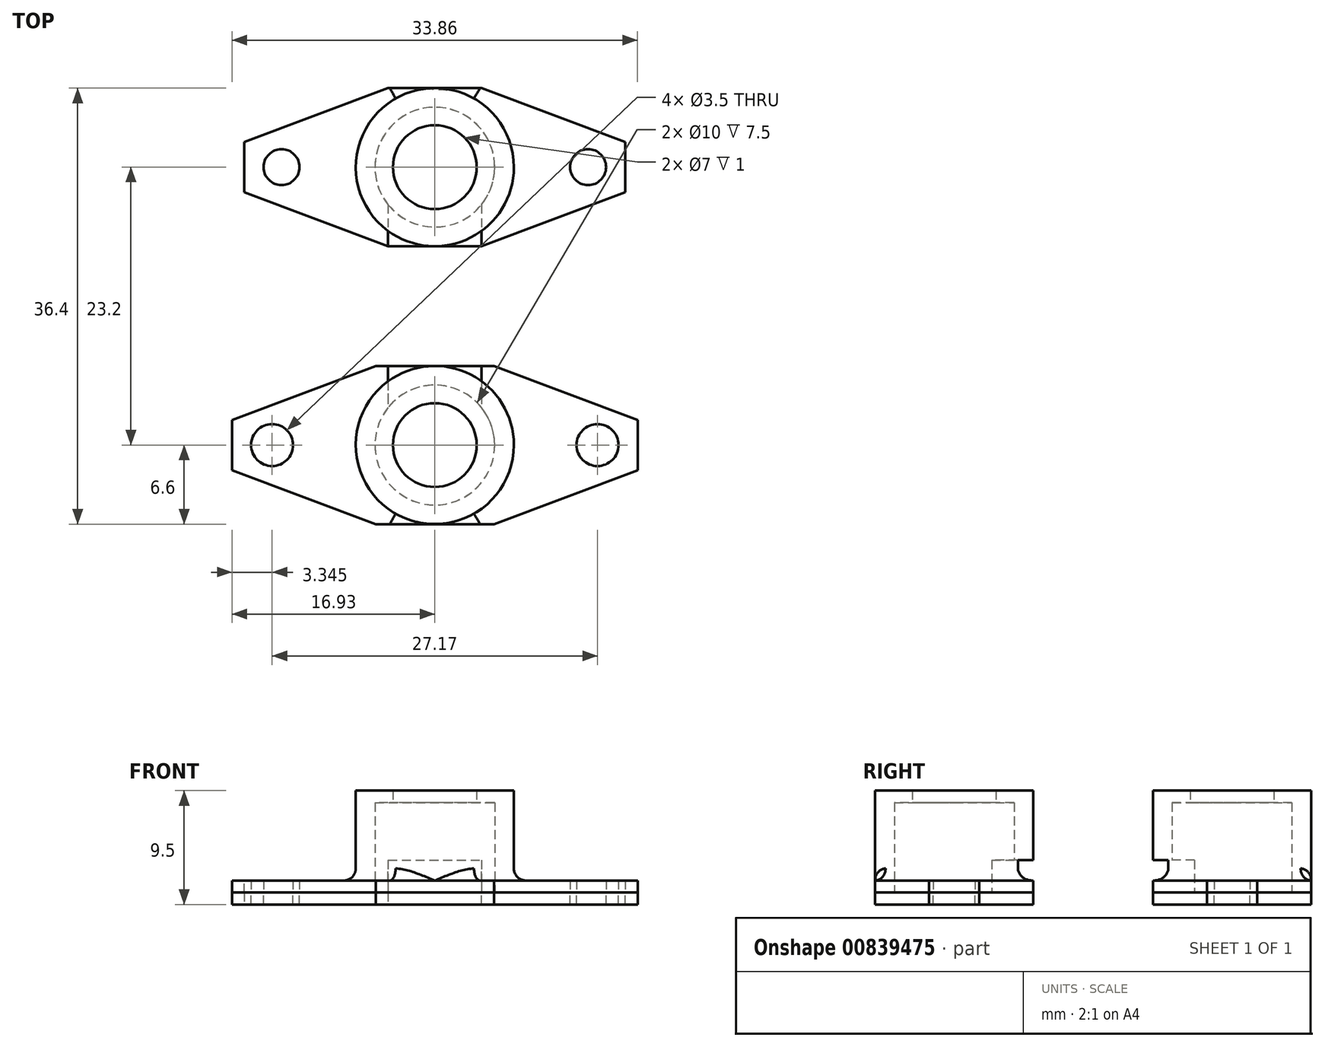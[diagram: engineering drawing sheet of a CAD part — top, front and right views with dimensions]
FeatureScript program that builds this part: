
annotation { "Feature Type Name" : "Feature", "Feature Type Description" : "" }
export const myFeature = defineFeature(function(context is Context, id is Id, definition is map)
    precondition{}
    {
        {
            var Q0;
            Q0=qCreatedBy(makeId("Top.planeOp"),FACE);
            var sketch = newSketch(context, id + "F0", { "sketchPlane" : qUnion([Q0])});
            skLineSegment(sketch, "E0.bottom", {"start": v(-15.9, 5) * mm, "end": v(15.9, 5) * mm});
            skLineSegment(sketch, "E0.top", {"start": v(-15.9, 18.2) * mm, "end": v(15.9, 18.2) * mm});
            skLineSegment(sketch, "E0.left", {"start": v(-15.9, 5) * mm, "end": v(-15.9, 18.2) * mm});
            skLineSegment(sketch, "E0.right", {"start": v(15.9, 5) * mm, "end": v(15.9, 18.2) * mm});
            skCircle(sketch, "E1", {"center": v(-12.8, 11.6) * mm, "radius": 1.5 * mm});
            skCircle(sketch, "E2", {"center": v(12.8, 11.6) * mm, "radius": 1.5 * mm});
            skCircle(sketch, "E3", {"center": v(-13.59, -11.6) * mm, "radius": 1.75 * mm});
            skCircle(sketch, "E4", {"center": v(13.59, -11.6) * mm, "radius": 1.75 * mm});
            skCircle(sketch, "E5", {"center": v(0, -11.6) * mm, "radius": 5 * mm});
            skCircle(sketch, "E6", {"center": v(0, 11.6) * mm, "radius": 5 * mm});
            skPoint(sketch, "E7", {"position": v(-15.9, 11.6) * mm});
            skLineSegment(sketch, "E8.bottom", {"start": v(-16.94, -18.2) * mm, "end": v(16.94, -18.2) * mm});
            skLineSegment(sketch, "E8.top", {"start": v(-16.94, -5) * mm, "end": v(16.94, -5) * mm});
            skLineSegment(sketch, "E8.left", {"start": v(-16.94, -18.2) * mm, "end": v(-16.94, -5) * mm});
            skLineSegment(sketch, "E8.right", {"start": v(16.94, -18.2) * mm, "end": v(16.94, -5) * mm});
            skCircle(sketch, "E9", {"center": v(0, 11.6) * mm, "radius": 6.6 * mm});
            skCircle(sketch, "E10", {"center": v(0, -11.6) * mm, "radius": 6.6 * mm});
            skSolve(sketch);
        }
        {
            var Q0;
            Q0=makeQuery(id+"F0.imprint","IMPRINT",FACE,{"disambiguationData":[TD([[makeQuery(id+"F0.imprint","IMPRINT",EDGE,{"derivedFrom":sQuery(id+"F0.wireOp",EDGE,"E0.bottom")}),1.0]])]});
            var Q1;
            Q1=makeQuery(id+"F0.imprint","IMPRINT",FACE,{"disambiguationData":[TD([[makeQuery(id+"F0.imprint","IMPRINT",EDGE,{"derivedFrom":sQuery(id+"F0.wireOp",EDGE,"E3")}),-1.0]])]});
            var Q2;
            Q2=makeQuery(id+"F0.imprint","IMPRINT",FACE,{"disambiguationData":[TD([[makeQuery(id+"F0.imprint","IMPRINT",EDGE,{"derivedFrom":sQuery(id+"F0.wireOp",EDGE,"E6")}),-1.0]])]});
            var Q3;
            Q3=makeQuery(id+"F0.imprint","IMPRINT",FACE,{"disambiguationData":[TD([[makeQuery(id+"F0.imprint","IMPRINT",EDGE,{"derivedFrom":sQuery(id+"F0.wireOp",EDGE,"E5")}),-1.0]])]});
            var Q4;
            Q4=makeQuery(id+"F0.imprint","IMPRINT",FACE,{"disambiguationData":[TD([[makeQuery(id+"F0.imprint","IMPRINT",EDGE,{"derivedFrom":sQuery(id+"F0.wireOp",EDGE,"E4")}),-1.0]])]});
            extrude(context, id + "F1", {"entities" : qUnion([Q0, Q1, Q2, Q3, Q4]), "depth" : 1 * mm, "offsetDistance" : 25 * mm});
        }
        {
            var Q0;
            Q0=makeQuery(id+"F1.opExtrude","SWEPT_EDGE",EDGE,{"disambiguationData":[OSD([sQuery(id+"F0.wireOp",EDGE,"E0.top"),sQuery(id+"F0.wireOp",EDGE,"E0.left")])]});
            var Q1;
            Q1=makeQuery(id+"F1.opExtrude","SWEPT_EDGE",EDGE,{"disambiguationData":[OSD([sQuery(id+"F0.wireOp",EDGE,"E0.bottom"),sQuery(id+"F0.wireOp",EDGE,"E0.left")])]});
            var Q2;
            Q2=makeQuery(id+"F1.opExtrude","SWEPT_EDGE",EDGE,{"disambiguationData":[OSD([sQuery(id+"F0.wireOp",EDGE,"E8.top"),sQuery(id+"F0.wireOp",EDGE,"E8.left")])]});
            var Q3;
            Q3=makeQuery(id+"F1.opExtrude","SWEPT_EDGE",EDGE,{"disambiguationData":[OSD([sQuery(id+"F0.wireOp",EDGE,"E8.bottom"),sQuery(id+"F0.wireOp",EDGE,"E8.left")])]});
            var Q4;
            Q4=makeQuery(id+"F1.opExtrude","SWEPT_EDGE",EDGE,{"disambiguationData":[OSD([sQuery(id+"F0.wireOp",EDGE,"E0.top"),sQuery(id+"F0.wireOp",EDGE,"E0.right")])]});
            var Q5;
            Q5=makeQuery(id+"F1.opExtrude","SWEPT_EDGE",EDGE,{"disambiguationData":[OSD([sQuery(id+"F0.wireOp",EDGE,"E0.bottom"),sQuery(id+"F0.wireOp",EDGE,"E0.right")])]});
            var Q6;
            Q6=makeQuery(id+"F1.opExtrude","SWEPT_EDGE",EDGE,{"disambiguationData":[OSD([sQuery(id+"F0.wireOp",EDGE,"E8.top"),sQuery(id+"F0.wireOp",EDGE,"E8.right")])]});
            var Q7;
            Q7=makeQuery(id+"F1.opExtrude","SWEPT_EDGE",EDGE,{"disambiguationData":[OSD([sQuery(id+"F0.wireOp",EDGE,"E8.bottom"),sQuery(id+"F0.wireOp",EDGE,"E8.right")])]});
            chamfer(context, id + "F2", {"entities" : qUnion([Q0, Q1, Q2, Q3, Q4, Q5, Q6, Q7]), "chamferType" : ChamferType.TWO_OFFSETS, "width1" : 4.5 * mm, "oppositeDirection" : false, "width2" : 12 * mm, "tangentPropagation" : true});
        }
        {
            var Q0;
            Q0=makeQuery(id+"F0.imprint","IMPRINT",FACE,{"disambiguationData":[TD([[makeQuery(id+"F0.imprint","IMPRINT",EDGE,{"derivedFrom":sQuery(id+"F0.wireOp",EDGE,"E5")}),-1.0]])]});
            var Q1;
            Q1=makeQuery(id+"F0.imprint","IMPRINT",FACE,{"disambiguationData":[TD([[makeQuery(id+"F0.imprint","IMPRINT",EDGE,{"derivedFrom":sQuery(id+"F0.wireOp",EDGE,"E6")}),-1.0]])]});
            extrude(context, id + "F3", {"entities" : qUnion([Q0, Q1]), "operationType" : NewBodyOperationType.ADD, "depth" : 7.5 * mm, "offsetDistance" : 25 * mm});
        }
        {
            var Q0;
            Q0=makeQuery(id+"F3.boolean.opBoolean","INTERSECT",EDGE,{"disambiguationData":[OD(1.0)],"derivedFrom":[makeQuery(id+"F1.opExtrude","CAP_FACE",FACE,{"disambiguationData":[OSD([sQuery(id+"F0.wireOp",EDGE,"E3"),sQuery(id+"F0.wireOp",EDGE,"E4"),sQuery(id+"F0.wireOp",EDGE,"E5"),sQuery(id+"F0.wireOp",EDGE,"E8.bottom"),sQuery(id+"F0.wireOp",EDGE,"E8.top"),sQuery(id+"F0.wireOp",EDGE,"E8.left"),sQuery(id+"F0.wireOp",EDGE,"E8.right")])],"isStart":false}),makeQuery(id+"F3.opExtrude","SWEPT_FACE",FACE,{"disambiguationData":[OSD([sQuery(id+"F0.wireOp",EDGE,"E10")])]})]});
            var Q1;
            Q1=makeQuery(id+"F3.boolean.opBoolean","INTERSECT",EDGE,{"disambiguationData":[OD(0.0)],"derivedFrom":[makeQuery(id+"F1.opExtrude","CAP_FACE",FACE,{"disambiguationData":[OSD([sQuery(id+"F0.wireOp",EDGE,"E3"),sQuery(id+"F0.wireOp",EDGE,"E4"),sQuery(id+"F0.wireOp",EDGE,"E5"),sQuery(id+"F0.wireOp",EDGE,"E8.bottom"),sQuery(id+"F0.wireOp",EDGE,"E8.top"),sQuery(id+"F0.wireOp",EDGE,"E8.left"),sQuery(id+"F0.wireOp",EDGE,"E8.right")])],"isStart":false}),makeQuery(id+"F3.opExtrude","SWEPT_FACE",FACE,{"disambiguationData":[OSD([sQuery(id+"F0.wireOp",EDGE,"E10")])]})]});
            var Q2;
            Q2=makeQuery(id+"F3.boolean.opBoolean","INTERSECT",EDGE,{"disambiguationData":[OD(0.0)],"derivedFrom":[makeQuery(id+"F1.opExtrude","CAP_FACE",FACE,{"disambiguationData":[OSD([sQuery(id+"F0.wireOp",EDGE,"E0.bottom"),sQuery(id+"F0.wireOp",EDGE,"E0.top"),sQuery(id+"F0.wireOp",EDGE,"E0.left"),sQuery(id+"F0.wireOp",EDGE,"E0.right"),sQuery(id+"F0.wireOp",EDGE,"E1"),sQuery(id+"F0.wireOp",EDGE,"E2"),sQuery(id+"F0.wireOp",EDGE,"E6")])],"isStart":false}),makeQuery(id+"F3.opExtrude","SWEPT_FACE",FACE,{"disambiguationData":[OSD([sQuery(id+"F0.wireOp",EDGE,"E9")])]})]});
            var Q3;
            Q3=makeQuery(id+"F3.boolean.opBoolean","INTERSECT",EDGE,{"disambiguationData":[OD(1.0)],"derivedFrom":[makeQuery(id+"F1.opExtrude","CAP_FACE",FACE,{"disambiguationData":[OSD([sQuery(id+"F0.wireOp",EDGE,"E0.bottom"),sQuery(id+"F0.wireOp",EDGE,"E0.top"),sQuery(id+"F0.wireOp",EDGE,"E0.left"),sQuery(id+"F0.wireOp",EDGE,"E0.right"),sQuery(id+"F0.wireOp",EDGE,"E1"),sQuery(id+"F0.wireOp",EDGE,"E2"),sQuery(id+"F0.wireOp",EDGE,"E6")])],"isStart":false}),makeQuery(id+"F3.opExtrude","SWEPT_FACE",FACE,{"disambiguationData":[OSD([sQuery(id+"F0.wireOp",EDGE,"E9")])]})]});
            fillet(context, id + "F4", {"entities" : qUnion([Q0, Q1, Q2, Q3]), "radius" : 1 * mm, "tangentPropagation" : true, "allowEdgeOverflow" : false});
        }
        {
            var Q0;
            Q0=makeQuery(id+"F3.opExtrude","CAP_FACE",FACE,{"disambiguationData":[OSD([sQuery(id+"F0.wireOp",EDGE,"E6"),sQuery(id+"F0.wireOp",EDGE,"E9")])],"isStart":false});
            var sketch = newSketch(context, id + "F5", { "sketchPlane" : qUnion([Q0])});
            skCircle(sketch, "E11.0", {"center": v(0, 11.6) * mm, "radius": 6.6 * mm});
            skCircle(sketch, "E12.0", {"center": v(0, -11.6) * mm, "radius": 6.6 * mm});
            skCircle(sketch, "E13", {"center": v(0, 11.6) * mm, "radius": 3.5 * mm});
            skCircle(sketch, "E14", {"center": v(0, -11.6) * mm, "radius": 3.5 * mm});
            skSolve(sketch);
        }
        {
            var Q0;
            Q0=makeQuery(id+"F5.imprint","IMPRINT",FACE,{"disambiguationData":[TD([[makeQuery(id+"F5.imprint","IMPRINT",EDGE,{"derivedFrom":sQuery(id+"F5.wireOp",EDGE,"E11.0")}),1.0]])]});
            var Q1;
            Q1=makeQuery(id+"F5.imprint","IMPRINT",FACE,{"disambiguationData":[TD([[makeQuery(id+"F5.imprint","IMPRINT",EDGE,{"derivedFrom":sQuery(id+"F5.wireOp",EDGE,"E13")}),-1.0]])]});
            var Q2;
            Q2=makeQuery(id+"F5.imprint","IMPRINT",FACE,{"disambiguationData":[TD([[makeQuery(id+"F5.imprint","IMPRINT",EDGE,{"derivedFrom":sQuery(id+"F5.wireOp",EDGE,"E12.0")}),1.0]])]});
            extrude(context, id + "F6", {"entities" : qUnion([Q0, Q1, Q2]), "operationType" : NewBodyOperationType.ADD, "depth" : 1 * mm, "offsetDistance" : 25 * mm});
        }
        {
            var Q0;
            Q0=qCreatedBy(makeId("Front.planeOp"),FACE);
            var sketch = newSketch(context, id + "F7", { "sketchPlane" : qUnion([Q0])});
            skLineSegment(sketch, "E15.0", {"start": v(-3.9, 1.5) * mm, "end": v(-3.9, 0) * mm, "construction": true});
            skLineSegment(sketch, "E16.0", {"start": v(3.9, 0) * mm, "end": v(3.9, 1.5) * mm, "construction": true});
            skPoint(sketch, "E17.0", {"position": v(0, 1.2) * mm});
            skLineSegment(sketch, "E18.bottom", {"start": v(-3.9, 0) * mm, "end": v(3.9, 0) * mm});
            skLineSegment(sketch, "E18.top", {"start": v(-3.9, 2.7) * mm, "end": v(3.9, 2.7) * mm});
            skLineSegment(sketch, "E18.left", {"start": v(-3.9, 0) * mm, "end": v(-3.9, 2.7) * mm});
            skLineSegment(sketch, "E18.right", {"start": v(3.9, 0) * mm, "end": v(3.9, 2.7) * mm});
            skLineSegment(sketch, "E19.0", {"start": v(-5, 0) * mm, "end": v(5, 0) * mm, "construction": true});
            skSolve(sketch);
        }
        {
            var Q0;
            Q0=makeQuery(id+"F7.imprint","IMPRINT",FACE,{"disambiguationData":[TD([[makeQuery(id+"F7.imprint","IMPRINT",EDGE,{"derivedFrom":sQuery(id+"F7.wireOp",EDGE,"mN3EGyrj-7LLR-joQA-lNur-RmMEQnrWh7OX.bottom")}),-1.0]])]});
            var Q1;
            Q1=makeQuery(id+"F7.imprint","IMPRINT",FACE,{"disambiguationData":[TD([[makeQuery(id+"F7.imprint","IMPRINT",EDGE,{"derivedFrom":sQuery(id+"F7.wireOp",EDGE,"E18.bottom")}),1.0]])]});
            extrude(context, id + "F8", {"entities" : qUnion([Q0, Q1]), "operationType" : NewBodyOperationType.REMOVE, "endBound" : BoundingType.SYMMETRIC, "oppositeDirection" : true, "depth" : 24 * mm, "offsetDistance" : 25 * mm});
        }
        {
            var Q0;
            Q0=makeQuery(id+"F0.imprint","IMPRINT",FACE,{"disambiguationData":[TD([[makeQuery(id+"F0.imprint","IMPRINT",EDGE,{"derivedFrom":sQuery(id+"F0.wireOp",EDGE,"E4")}),-1.0]])]});
            var Q1;
            Q1=makeQuery(id+"F0.imprint","IMPRINT",FACE,{"disambiguationData":[TD([[makeQuery(id+"F0.imprint","IMPRINT",EDGE,{"derivedFrom":sQuery(id+"F0.wireOp",EDGE,"E5")}),-1.0]])]});
            var Q2;
            Q2=makeQuery(id+"F0.imprint","IMPRINT",FACE,{"disambiguationData":[TD([[makeQuery(id+"F0.imprint","IMPRINT",EDGE,{"derivedFrom":sQuery(id+"F0.wireOp",EDGE,"E5")}),1.0]])]});
            var Q3;
            Q3=makeQuery(id+"F0.imprint","IMPRINT",FACE,{"disambiguationData":[TD([[makeQuery(id+"F0.imprint","IMPRINT",EDGE,{"derivedFrom":sQuery(id+"F0.wireOp",EDGE,"E3")}),-1.0]])]});
            var Q4;
            {var subQ0=sQuery(id+"F0.wireOp",EDGE,"E0.left");Q4=makeQuery(id+"F0.imprint","IMPRINT",FACE,{"disambiguationData":[TD([[makeQuery(id+"F0.imprint","IMPRINT",EDGE,{"derivedFrom":subQ0}),-1.0]])]});}
            var Q5;
            Q5=makeQuery(id+"F0.imprint","IMPRINT",FACE,{"disambiguationData":[TD([[makeQuery(id+"F0.imprint","IMPRINT",EDGE,{"derivedFrom":sQuery(id+"F0.wireOp",EDGE,"E6")}),-1.0]])]});
            var Q6;
            {var subQ0=sQuery(id+"F0.wireOp",EDGE,"E0.right");Q6=makeQuery(id+"F0.imprint","IMPRINT",FACE,{"disambiguationData":[TD([[makeQuery(id+"F0.imprint","IMPRINT",EDGE,{"derivedFrom":subQ0}),1.0]])]});}
            var Q7;
            Q7=makeQuery(id+"F0.imprint","IMPRINT",FACE,{"disambiguationData":[TD([[makeQuery(id+"F0.imprint","IMPRINT",EDGE,{"derivedFrom":sQuery(id+"F0.wireOp",EDGE,"E6")}),1.0]])]});
            extrude(context, id + "F9", {"entities" : qUnion([Q0, Q1, Q2, Q3, Q4, Q5, Q6, Q7]), "oppositeDirection" : true, "depth" : 1 * mm, "offsetDistance" : 25 * mm});
        }
        {
            var Q0;
            Q0=makeQuery(id+"F9.opExtrude","SWEPT_EDGE",EDGE,{"disambiguationData":[OSD([sQuery(id+"F0.wireOp",EDGE,"E0.bottom"),sQuery(id+"F0.wireOp",EDGE,"E0.left")])]});
            var Q1;
            Q1=makeQuery(id+"F9.opExtrude","SWEPT_EDGE",EDGE,{"disambiguationData":[OSD([sQuery(id+"F0.wireOp",EDGE,"E0.top"),sQuery(id+"F0.wireOp",EDGE,"E0.left")])]});
            var Q2;
            Q2=makeQuery(id+"F9.opExtrude","SWEPT_EDGE",EDGE,{"disambiguationData":[OSD([sQuery(id+"F0.wireOp",EDGE,"E0.bottom"),sQuery(id+"F0.wireOp",EDGE,"E0.right")])]});
            var Q3;
            Q3=makeQuery(id+"F9.opExtrude","SWEPT_EDGE",EDGE,{"disambiguationData":[OSD([sQuery(id+"F0.wireOp",EDGE,"E0.top"),sQuery(id+"F0.wireOp",EDGE,"E0.right")])]});
            var Q4;
            Q4=makeQuery(id+"F9.opExtrude","SWEPT_EDGE",EDGE,{"disambiguationData":[OSD([sQuery(id+"F0.wireOp",EDGE,"E8.top"),sQuery(id+"F0.wireOp",EDGE,"E8.right")])]});
            var Q5;
            Q5=makeQuery(id+"F9.opExtrude","SWEPT_EDGE",EDGE,{"disambiguationData":[OSD([sQuery(id+"F0.wireOp",EDGE,"E8.bottom"),sQuery(id+"F0.wireOp",EDGE,"E8.right")])]});
            var Q6;
            Q6=makeQuery(id+"F9.opExtrude","SWEPT_EDGE",EDGE,{"disambiguationData":[OSD([sQuery(id+"F0.wireOp",EDGE,"E8.top"),sQuery(id+"F0.wireOp",EDGE,"E8.left")])]});
            var Q7;
            Q7=makeQuery(id+"F9.opExtrude","SWEPT_EDGE",EDGE,{"disambiguationData":[OSD([sQuery(id+"F0.wireOp",EDGE,"E8.bottom"),sQuery(id+"F0.wireOp",EDGE,"E8.left")])]});
            chamfer(context, id + "F10", {"entities" : qUnion([Q0, Q1, Q2, Q3, Q4, Q5, Q6, Q7]), "chamferType" : ChamferType.TWO_OFFSETS, "width1" : 4.5 * mm, "oppositeDirection" : false, "width2" : 12 * mm, "tangentPropagation" : true});
        }
    });
